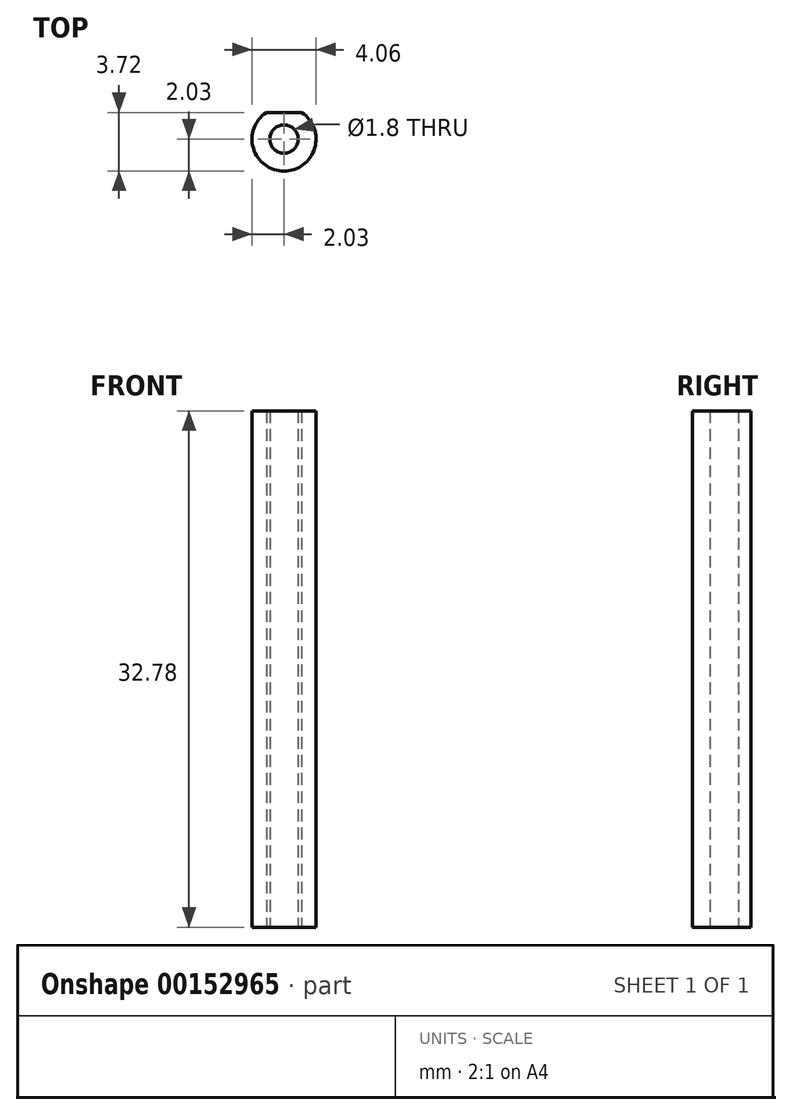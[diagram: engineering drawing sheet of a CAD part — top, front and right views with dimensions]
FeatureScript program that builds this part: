
annotation { "Feature Type Name" : "Feature", "Feature Type Description" : "" }
export const myFeature = defineFeature(function(context is Context, id is Id, definition is map)
    precondition{}
    {
        {
            var Q0;
            Q0=qCreatedBy(makeId("Top.planeOp"),FACE);
            var sketch = newSketch(context, id + "F0", { "sketchPlane" : qUnion([Q0])});
            skArc(sketch, "E0", {"start": v(-1.12, 1.7) * mm, "mid": v(0, -2.03) * mm, "end": v(1.12, 1.7) * mm});
            skLineSegment(sketch, "E1", {"start": v(-1.12, 1.7) * mm, "end": v(1.12, 1.7) * mm});
            skLineSegment(sketch, "E2", {"start": v(0, 0) * mm, "end": v(0, 1.7) * mm, "construction": true});
            skCircle(sketch, "E3", {"center": v(0, 0) * mm, "radius": 0.9 * mm});
            skSolve(sketch);
        }
        {
            var Q0;
            Q0 = qSketchRegion(id + "F0", true);
            extrude(context, id + "F1", {"entities" : qUnion([Q0]), "depth" : 32.78 * mm});
        }
    });
